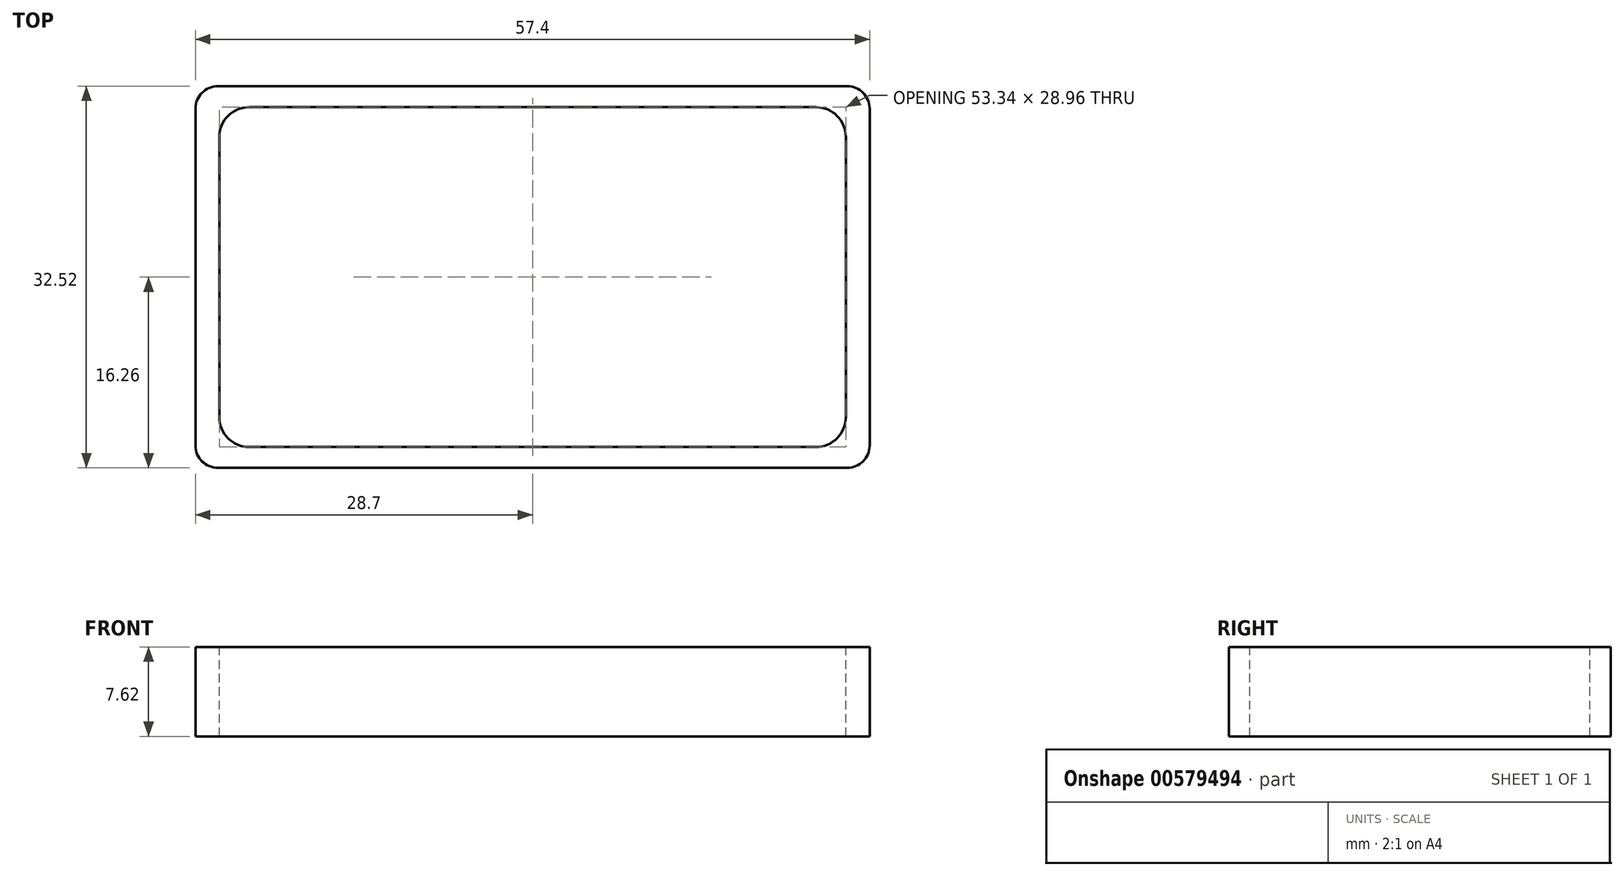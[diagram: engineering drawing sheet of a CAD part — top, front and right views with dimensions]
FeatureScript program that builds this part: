
annotation { "Feature Type Name" : "Feature", "Feature Type Description" : "" }
export const myFeature = defineFeature(function(context is Context, id is Id, definition is map)
    precondition{}
    {
        {
            var Q0;
            Q0=qCreatedBy(makeId("Top.planeOp"),FACE);
            var sketch = newSketch(context, id + "F0", { "sketchPlane" : qUnion([Q0])});
            skLineSegment(sketch, "E0.bottom", {"start": v(24.13, 14.48) * mm, "end": v(-24.13, 14.48) * mm});
            skLineSegment(sketch, "E0.top", {"start": v(24.13, -14.48) * mm, "end": v(-24.13, -14.48) * mm});
            skLineSegment(sketch, "E0.left", {"start": v(26.67, 11.94) * mm, "end": v(26.67, -11.94) * mm});
            skLineSegment(sketch, "E0.right", {"start": v(-26.67, 11.94) * mm, "end": v(-26.67, -11.94) * mm});
            skPoint(sketch, "E0.middle", {"position": v(0, 0) * mm});
            skLineSegment(sketch, "E1.bottom", {"start": v(26.8, 16.26) * mm, "end": v(-26.8, 16.26) * mm});
            skLineSegment(sketch, "E1.top", {"start": v(26.8, -16.26) * mm, "end": v(-26.8, -16.26) * mm});
            skLineSegment(sketch, "E1.left", {"start": v(28.7, 14.35) * mm, "end": v(28.7, -14.35) * mm});
            skLineSegment(sketch, "E1.right", {"start": v(-28.7, 14.35) * mm, "end": v(-28.7, -14.35) * mm});
            skPoint(sketch, "E2.visualSharp", {"position": v(-26.67, 14.48) * mm});
            skArc(sketch, "E2.filletArc", {"start": v(-24.13, 14.48) * mm, "mid": v(-25.93, 13.73) * mm, "end": v(-26.67, 11.94) * mm});
            skPoint(sketch, "E3.visualSharp", {"position": v(-26.67, -14.48) * mm});
            skArc(sketch, "E3.filletArc", {"start": v(-26.67, -11.94) * mm, "mid": v(-25.93, -13.73) * mm, "end": v(-24.13, -14.48) * mm});
            skPoint(sketch, "E4.visualSharp", {"position": v(26.67, -14.48) * mm});
            skArc(sketch, "E4.filletArc", {"start": v(24.13, -14.48) * mm, "mid": v(25.93, -13.73) * mm, "end": v(26.67, -11.94) * mm});
            skPoint(sketch, "E5.visualSharp", {"position": v(26.67, 14.48) * mm});
            skArc(sketch, "E5.filletArc", {"start": v(26.67, 11.94) * mm, "mid": v(25.93, 13.73) * mm, "end": v(24.13, 14.48) * mm});
            skPoint(sketch, "E6.visualSharp", {"position": v(-28.7, 16.26) * mm});
            skArc(sketch, "E6.filletArc", {"start": v(-26.8, 16.26) * mm, "mid": v(-28.14, 15.7) * mm, "end": v(-28.7, 14.35) * mm});
            skPoint(sketch, "E7.visualSharp", {"position": v(28.7, 16.26) * mm});
            skArc(sketch, "E7.filletArc", {"start": v(28.7, 14.35) * mm, "mid": v(28.14, 15.7) * mm, "end": v(26.8, 16.26) * mm});
            skPoint(sketch, "E8.visualSharp", {"position": v(28.7, -16.26) * mm});
            skArc(sketch, "E8.filletArc", {"start": v(26.8, -16.26) * mm, "mid": v(28.14, -15.7) * mm, "end": v(28.7, -14.35) * mm});
            skPoint(sketch, "E9.visualSharp", {"position": v(-28.7, -16.26) * mm});
            skArc(sketch, "E9.filletArc", {"start": v(-28.7, -14.35) * mm, "mid": v(-28.14, -15.7) * mm, "end": v(-26.8, -16.26) * mm});
            skSolve(sketch);
        }
        {
            var Q0;
            Q0=makeQuery(id+"F0.imprint","IMPRINT",FACE,{"disambiguationData":[TD([[makeQuery(id+"F0.imprint","IMPRINT",EDGE,{"derivedFrom":sQuery(id+"F0.wireOp",EDGE,"E0.bottom")}),-1.0]])]});
            extrude(context, id + "F1", {"entities" : qUnion([Q0]), "oppositeDirection" : true, "depth" : 7.62 * mm, "offsetDistance" : 25.4 * mm});
        }
    });
